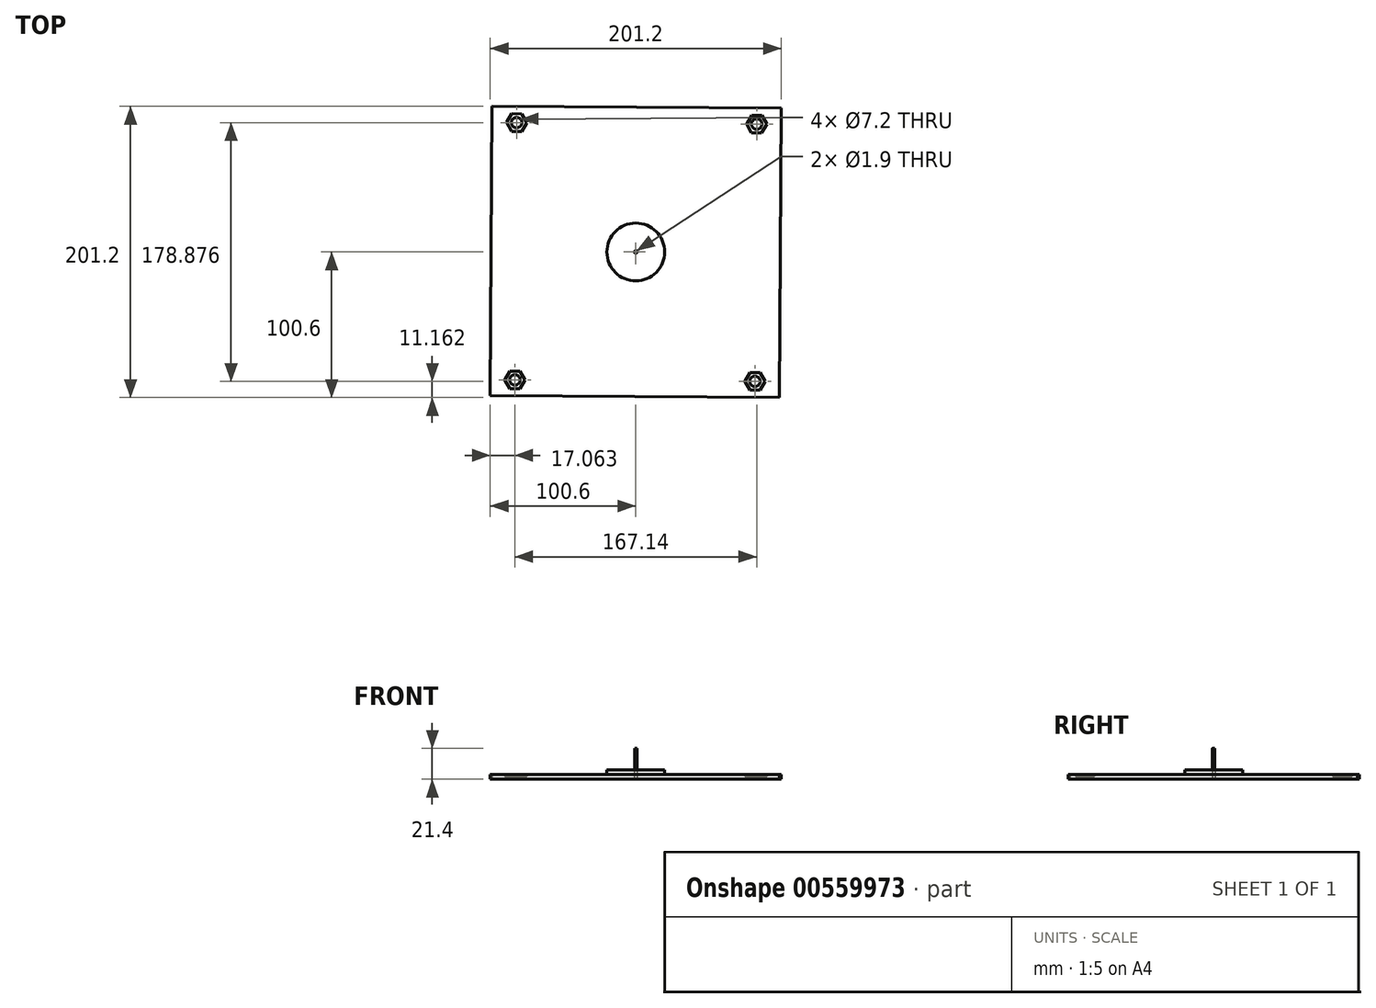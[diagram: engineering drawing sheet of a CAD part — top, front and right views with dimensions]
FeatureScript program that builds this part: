
annotation { "Feature Type Name" : "Feature", "Feature Type Description" : "" }
export const myFeature = defineFeature(function(context is Context, id is Id, definition is map)
    precondition{}
    {
        {
            var Q0;
            Q0=qCreatedBy(makeId("Top.planeOp"),FACE);
            var sketch = newSketch(context, id + "F0", { "sketchPlane" : qUnion([Q0])});
            skLineSegment(sketch, "E0.bottom", {"start": v(-99.4, 100.6) * mm, "end": v(100.6, 99.4) * mm});
            skLineSegment(sketch, "E0.top", {"start": v(-100.6, -99.4) * mm, "end": v(99.4, -100.6) * mm});
            skLineSegment(sketch, "E0.left", {"start": v(-99.4, 100.6) * mm, "end": v(-100.6, -99.4) * mm});
            skLineSegment(sketch, "E0.right", {"start": v(100.6, 99.4) * mm, "end": v(99.4, -100.6) * mm});
            skCircle(sketch, "E1.cCircle", {"center": v(-83.54, -88.43) * mm, "radius": 6.06 * mm, "construction": true});
            skLineSegment(sketch, "E1.0", {"start": v(-90.54, -88.4) * mm, "end": v(-87.07, -94.47) * mm});
            skLineSegment(sketch, "E1.1", {"start": v(-87, -82.35) * mm, "end": v(-90.54, -88.4) * mm});
            skLineSegment(sketch, "E1.2", {"start": v(-80, -82.4) * mm, "end": v(-87, -82.35) * mm});
            skLineSegment(sketch, "E1.3", {"start": v(-76.54, -88.48) * mm, "end": v(-80, -82.4) * mm});
            skLineSegment(sketch, "E1.4", {"start": v(-80.07, -94.52) * mm, "end": v(-76.54, -88.48) * mm});
            skLineSegment(sketch, "E1.5", {"start": v(-87.07, -94.47) * mm, "end": v(-80.07, -94.52) * mm});
            skPoint(sketch, "E1.0.midPoint", {"position": v(-88.8, -91.43) * mm});
            skCircle(sketch, "E2", {"center": v(-83.54, -88.43) * mm, "radius": 3.6 * mm});
            skCircle(sketch, "E3.cCircle", {"center": v(-82.4, 89.44) * mm, "radius": 6.06 * mm, "construction": true});
            skLineSegment(sketch, "E3.0", {"start": v(-75.4, 89.4) * mm, "end": v(-78.93, 83.35) * mm});
            skLineSegment(sketch, "E3.1", {"start": v(-78.93, 83.35) * mm, "end": v(-85.93, 83.4) * mm});
            skLineSegment(sketch, "E3.2", {"start": v(-85.93, 83.4) * mm, "end": v(-89.4, 89.48) * mm});
            skLineSegment(sketch, "E3.3", {"start": v(-89.4, 89.48) * mm, "end": v(-85.86, 95.52) * mm});
            skLineSegment(sketch, "E3.4", {"start": v(-85.86, 95.52) * mm, "end": v(-78.86, 95.48) * mm});
            skLineSegment(sketch, "E3.5", {"start": v(-78.86, 95.48) * mm, "end": v(-75.4, 89.4) * mm});
            skPoint(sketch, "E3.0.midPoint", {"position": v(-77.16, 86.38) * mm});
            skCircle(sketch, "E4", {"center": v(-82.4, 89.44) * mm, "radius": 3.6 * mm});
            skCircle(sketch, "E5.cCircle", {"center": v(83.6, 88.43) * mm, "radius": 6.06 * mm, "construction": true});
            skLineSegment(sketch, "E5.0", {"start": v(90.6, 88.4) * mm, "end": v(87.07, 82.35) * mm});
            skLineSegment(sketch, "E5.1", {"start": v(87.07, 82.35) * mm, "end": v(80.07, 82.4) * mm});
            skLineSegment(sketch, "E5.2", {"start": v(80.07, 82.4) * mm, "end": v(76.6, 88.48) * mm});
            skLineSegment(sketch, "E5.3", {"start": v(76.6, 88.48) * mm, "end": v(80.14, 94.52) * mm});
            skLineSegment(sketch, "E5.4", {"start": v(80.14, 94.52) * mm, "end": v(87.14, 94.47) * mm});
            skLineSegment(sketch, "E5.5", {"start": v(87.14, 94.47) * mm, "end": v(90.6, 88.4) * mm});
            skPoint(sketch, "E5.0.midPoint", {"position": v(88.83, 85.37) * mm});
            skCircle(sketch, "E6", {"center": v(83.6, 88.43) * mm, "radius": 3.6 * mm});
            skCircle(sketch, "E7.cCircle", {"center": v(82.4, -89.44) * mm, "radius": 6.06 * mm, "construction": true});
            skLineSegment(sketch, "E7.0", {"start": v(89.4, -89.48) * mm, "end": v(85.86, -95.52) * mm});
            skLineSegment(sketch, "E7.1", {"start": v(85.86, -95.52) * mm, "end": v(78.86, -95.48) * mm});
            skLineSegment(sketch, "E7.2", {"start": v(78.86, -95.48) * mm, "end": v(75.4, -89.4) * mm});
            skLineSegment(sketch, "E7.3", {"start": v(75.4, -89.4) * mm, "end": v(78.93, -83.35) * mm});
            skLineSegment(sketch, "E7.4", {"start": v(78.93, -83.35) * mm, "end": v(85.93, -83.4) * mm});
            skLineSegment(sketch, "E7.5", {"start": v(85.93, -83.4) * mm, "end": v(89.4, -89.48) * mm});
            skPoint(sketch, "E7.0.midPoint", {"position": v(87.62, -92.5) * mm});
            skCircle(sketch, "E8", {"center": v(82.4, -89.44) * mm, "radius": 3.6 * mm});
            skCircle(sketch, "E9", {"center": v(0, 0) * mm, "radius": 0.95 * mm});
            skSolve(sketch);
        }
        {
            var Q0;
            Q0=makeQuery(id+"F0.imprint","IMPRINT",FACE,{"disambiguationData":[TD([[makeQuery(id+"F0.imprint","IMPRINT",EDGE,{"derivedFrom":sQuery(id+"F0.wireOp",EDGE,"E0.bottom")}),-1.0]])]});
            extrude(context, id + "F1", {"entities" : qUnion([Q0]), "depth" : 3.2 * mm});
        }
        {
            var Q0;
            Q0=makeQuery(id+"F0.imprint","IMPRINT",FACE,{"disambiguationData":[TD([[makeQuery(id+"F0.imprint","IMPRINT",EDGE,{"derivedFrom":sQuery(id+"F0.wireOp",EDGE,"E1.0")}),1.0]])]});
            var Q1;
            Q1=makeQuery(id+"F0.imprint","IMPRINT",FACE,{"disambiguationData":[TD([[makeQuery(id+"F0.imprint","IMPRINT",EDGE,{"derivedFrom":sQuery(id+"F0.wireOp",EDGE,"E3.0")}),-1.0]])]});
            var Q2;
            Q2=makeQuery(id+"F0.imprint","IMPRINT",FACE,{"disambiguationData":[TD([[makeQuery(id+"F0.imprint","IMPRINT",EDGE,{"derivedFrom":sQuery(id+"F0.wireOp",EDGE,"E7.0")}),-1.0]])]});
            var Q3;
            Q3=makeQuery(id+"F0.imprint","IMPRINT",FACE,{"disambiguationData":[TD([[makeQuery(id+"F0.imprint","IMPRINT",EDGE,{"derivedFrom":sQuery(id+"F0.wireOp",EDGE,"E5.0")}),-1.0]])]});
            extrude(context, id + "F2", {"entities" : qUnion([Q0, Q1, Q2, Q3]), "operationType" : NewBodyOperationType.ADD, "depth" : 2 * mm});
        }
        {
            var Q0;
            Q0=makeQuery(id+"F1.opExtrude","CAP_FACE",FACE,{"disambiguationData":[OSD([sQuery(id+"F0.wireOp",EDGE,"E0.bottom"),sQuery(id+"F0.wireOp",EDGE,"E0.top"),sQuery(id+"F0.wireOp",EDGE,"E0.left"),sQuery(id+"F0.wireOp",EDGE,"E0.right"),sQuery(id+"F0.wireOp",EDGE,"E1.0"),sQuery(id+"F0.wireOp",EDGE,"E1.1"),sQuery(id+"F0.wireOp",EDGE,"E1.2"),sQuery(id+"F0.wireOp",EDGE,"E1.3"),sQuery(id+"F0.wireOp",EDGE,"E1.4"),sQuery(id+"F0.wireOp",EDGE,"E1.5"),sQuery(id+"F0.wireOp",EDGE,"E3.0"),sQuery(id+"F0.wireOp",EDGE,"E3.1"),sQuery(id+"F0.wireOp",EDGE,"E3.2"),sQuery(id+"F0.wireOp",EDGE,"E3.3"),sQuery(id+"F0.wireOp",EDGE,"E3.4"),sQuery(id+"F0.wireOp",EDGE,"E3.5"),sQuery(id+"F0.wireOp",EDGE,"E5.0"),sQuery(id+"F0.wireOp",EDGE,"E5.1"),sQuery(id+"F0.wireOp",EDGE,"E5.2"),sQuery(id+"F0.wireOp",EDGE,"E5.3"),sQuery(id+"F0.wireOp",EDGE,"E5.4"),sQuery(id+"F0.wireOp",EDGE,"E5.5"),sQuery(id+"F0.wireOp",EDGE,"E7.0"),sQuery(id+"F0.wireOp",EDGE,"E7.1"),sQuery(id+"F0.wireOp",EDGE,"E7.2"),sQuery(id+"F0.wireOp",EDGE,"E7.3"),sQuery(id+"F0.wireOp",EDGE,"E7.4"),sQuery(id+"F0.wireOp",EDGE,"E7.5")])],"isStart":false});
            var sketch = newSketch(context, id + "F3", { "sketchPlane" : qUnion([Q0])});
            skCircle(sketch, "E10", {"center": v(0, 0) * mm, "radius": 20 * mm});
            skCircle(sketch, "E11", {"center": v(0, 0) * mm, "radius": 0.95 * mm});
            skSolve(sketch);
        }
        {
            var Q0;
            Q0=makeQuery(id+"F3.imprint","IMPRINT",FACE,{"disambiguationData":[TD([[makeQuery(id+"F3.imprint","IMPRINT",EDGE,{"derivedFrom":sQuery(id+"F3.wireOp",EDGE,"E10")}),1.0]])]});
            extrude(context, id + "F4", {"entities" : qUnion([Q0]), "depth" : 3.2 * mm});
        }
        {
            var Q0;
            Q0=makeQuery(id+"F4.opExtrude","CAP_FACE",FACE,{"disambiguationData":[OSD([sQuery(id+"F3.wireOp",EDGE,"E10"),sQuery(id+"F3.wireOp",EDGE,"E11")])],"isStart":false});
            var sketch = newSketch(context, id + "F5", { "sketchPlane" : qUnion([Q0])});
            skCircle(sketch, "E12", {"center": v(0, 0) * mm, "radius": 0.8 * mm});
            skSolve(sketch);
        }
        {
            var Q0;
            Q0=makeQuery(id+"F5.imprint","IMPRINT",FACE,{"disambiguationData":[TD([[makeQuery(id+"F5.imprint","IMPRINT",EDGE,{"derivedFrom":sQuery(id+"F5.wireOp",EDGE,"E12")}),1.0]])]});
            extrude(context, id + "F6", {"entities" : qUnion([Q0]), "depth" : 15 * mm, "offsetDistance" : 25 * mm});
        }
    });
